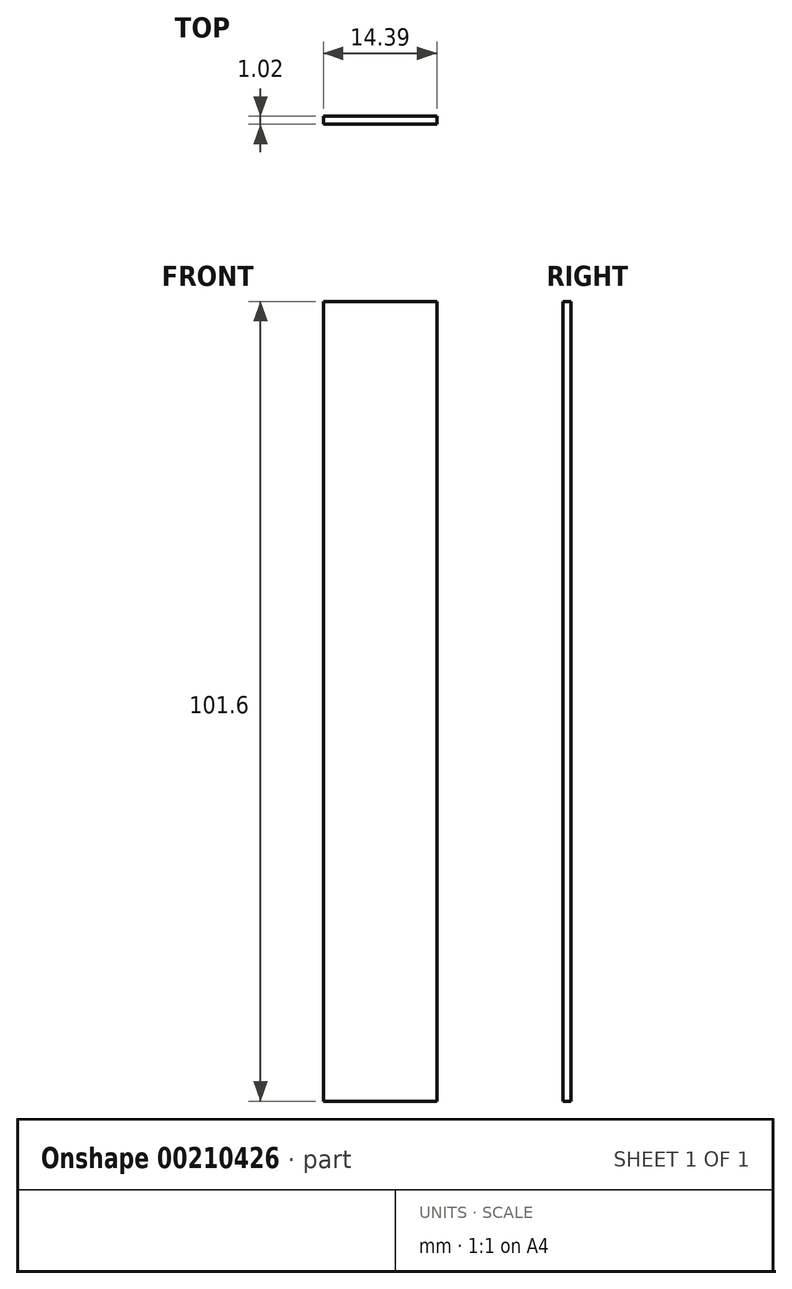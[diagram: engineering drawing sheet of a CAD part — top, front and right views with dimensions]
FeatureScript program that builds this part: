
annotation { "Feature Type Name" : "Feature", "Feature Type Description" : "" }
export const myFeature = defineFeature(function(context is Context, id is Id, definition is map)
    precondition{}
    {
        {
            var Q0;
            Q0=qCreatedBy(makeId("Front.planeOp"),FACE);
            var sketch = newSketch(context, id + "F0", { "sketchPlane" : qUnion([Q0])});
            skLineSegment(sketch, "E0.bottom", {"start": v(91.35, -85.75) * mm, "end": v(105.74, -85.75) * mm});
            skLineSegment(sketch, "E0.top", {"start": v(91.35, 15.85) * mm, "end": v(105.74, 15.85) * mm});
            skLineSegment(sketch, "E0.left", {"start": v(91.35, -85.75) * mm, "end": v(91.35, 15.85) * mm});
            skLineSegment(sketch, "E0.right", {"start": v(105.74, -85.75) * mm, "end": v(105.74, 15.85) * mm});
            skSolve(sketch);
        }
        {
            var Q0;
            Q0 = qSketchRegion(id + "F0", true);
            extrude(context, id + "F1", {"entities" : qUnion([Q0]), "depth" : 1.02 * mm});
        }
    });
